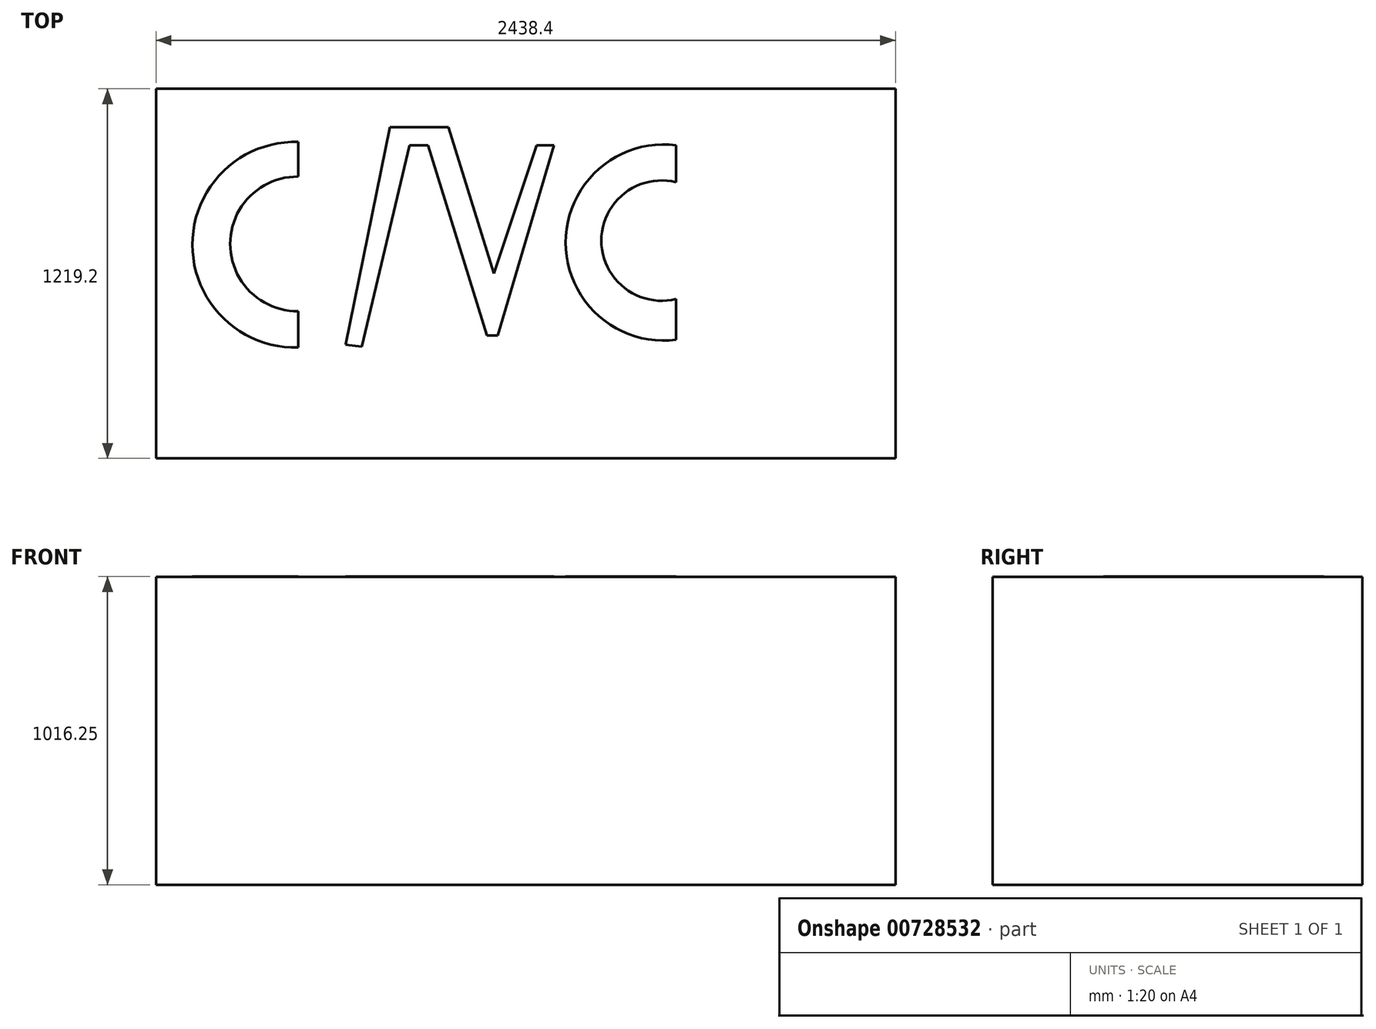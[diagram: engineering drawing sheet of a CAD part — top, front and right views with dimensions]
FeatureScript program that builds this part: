
annotation { "Feature Type Name" : "Feature", "Feature Type Description" : "" }
export const myFeature = defineFeature(function(context is Context, id is Id, definition is map)
    precondition{}
    {
        {
            var Q0;
            Q0=qCreatedBy(makeId("Top.planeOp"),FACE);
            var sketch = newSketch(context, id + "F0", { "sketchPlane" : qUnion([Q0])});
            skLineSegment(sketch, "E0.bottom", {"start": v(1219.2, 609.6) * mm, "end": v(-1219.2, 609.6) * mm});
            skLineSegment(sketch, "E0.top", {"start": v(1219.2, -609.6) * mm, "end": v(-1219.2, -609.6) * mm});
            skLineSegment(sketch, "E0.left", {"start": v(1219.2, 609.6) * mm, "end": v(1219.2, -609.6) * mm});
            skLineSegment(sketch, "E0.right", {"start": v(-1219.2, 609.6) * mm, "end": v(-1219.2, -609.6) * mm});
            skPoint(sketch, "E0.middle", {"position": v(0, 0) * mm});
            skSolve(sketch);
        }
        {
            var Q0;
            Q0 = qSketchRegion(id + "F0", true);
            extrude(context, id + "F1", {"entities" : qUnion([Q0]), "depth" : 1016 * mm, "offsetDistance" : 25.4 * mm});
        }
        {
            var Q0;
            Q0=makeQuery(id+"F1.opExtrude","CAP_FACE",FACE,{"disambiguationData":[OSD([sQuery(id+"F0.wireOp",EDGE,"E0.bottom"),sQuery(id+"F0.wireOp",EDGE,"E0.top"),sQuery(id+"F0.wireOp",EDGE,"E0.left"),sQuery(id+"F0.wireOp",EDGE,"E0.right")])],"isStart":false});
            var sketch = newSketch(context, id + "F2", { "sketchPlane" : qUnion([Q0])});
            skLineSegment(sketch, "E1", {"start": v(-750.4, 434.44) * mm, "end": v(-750.4, 320.04) * mm});
            skLineSegment(sketch, "E2", {"start": v(-750.4, -123.93) * mm, "end": v(-750.4, -243.78) * mm});
            skArc(sketch, "E3", {"start": v(-750.4, 320.04) * mm, "mid": v(-974.65, 98.05) * mm, "end": v(-750.4, -123.93) * mm});
            skArc(sketch, "E4", {"start": v(-750.4, 434.44) * mm, "mid": v(-1099.17, 95.33) * mm, "end": v(-750.4, -243.78) * mm});
            skLineSegment(sketch, "E5", {"start": v(-540.66, -241.05) * mm, "end": v(-382.69, 423.54) * mm});
            skLineSegment(sketch, "E6", {"start": v(-382.69, 423.54) * mm, "end": v(-322.4, 423.54) * mm});
            skLineSegment(sketch, "E7", {"start": v(-322.4, 423.54) * mm, "end": v(-128.05, -204.58) * mm});
            skLineSegment(sketch, "E8", {"start": v(-128.05, -204.58) * mm, "end": v(-92.81, -204.58) * mm});
            skLineSegment(sketch, "E9", {"start": v(-92.81, -204.58) * mm, "end": v(92.5, 423.54) * mm});
            skLineSegment(sketch, "E10", {"start": v(92.5, 423.54) * mm, "end": v(36.17, 423.54) * mm});
            skLineSegment(sketch, "E11", {"start": v(36.17, 423.54) * mm, "end": v(-104.97, 0) * mm});
            skLineSegment(sketch, "E12", {"start": v(-104.97, 0) * mm, "end": v(-254.54, 483.4) * mm});
            skLineSegment(sketch, "E13", {"start": v(-254.54, 483.4) * mm, "end": v(-447.8, 483.4) * mm});
            skLineSegment(sketch, "E14", {"start": v(-447.8, 483.4) * mm, "end": v(-593.6, -234.01) * mm});
            skLineSegment(sketch, "E15", {"start": v(-593.6, -234.01) * mm, "end": v(-540.66, -241.05) * mm});
            skLineSegment(sketch, "E16", {"start": v(495.94, 423.54) * mm, "end": v(495.94, 301.52) * mm});
            skLineSegment(sketch, "E17", {"start": v(495.94, -83.67) * mm, "end": v(495.94, -218.5) * mm});
            skArc(sketch, "E18", {"start": v(495.94, 301.52) * mm, "mid": v(249.37, 108.92) * mm, "end": v(495.94, -83.67) * mm});
            skArc(sketch, "E19", {"start": v(495.94, 423.54) * mm, "mid": v(131.7, 102.53) * mm, "end": v(495.94, -218.5) * mm});
            skSolve(sketch);
        }
        {
            var Q0;
            Q0 = qSketchRegion(id + "F2", true);
            extrude(context, id + "F3", {"entities" : qUnion([Q0]), "operationType" : NewBodyOperationType.ADD, "depth" : 0.25 * mm, "offsetDistance" : 25.4 * mm});
        }
    });
